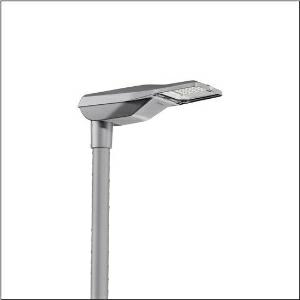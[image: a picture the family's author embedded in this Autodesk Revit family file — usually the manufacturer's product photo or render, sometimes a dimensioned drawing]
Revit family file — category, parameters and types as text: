
# Revit family: streetlight_sl_21_iq_micro___st1_5a_5xe1p41g08cb_60b9
name_source: partatom
category: Lighting Fixtures
units: mm (PartAtom-declared; Revit-internal decimal feet)

## family parameters
Cut with Voids When Loaded = No
Host = Face
Light Source = No
Part Type = Normal
Room Calculation Point = No
Round Connector Dimension = Use Diameter
Shared = No

## types (1)
- --- (1 x LED, 2930 lm, 19.4 W, 4000K)
    Apparent Load = 19 VA
    CIE Flux Codes = 22 53 95 100 100
    Color Rendering = 70
    Color Temperature = 4000K
    Default Elevation = 1800 mm
    Description = Streetlight SL 21 iQ micro, mast luminaire, primary light control with lens, of PMMA, primary optical cover: cover, of toughened safety glass, transparent, light distribution: ST1.5a, light emission: direct distribution, primary light characteristic: asymmetric, installation type: post-top, side-entry, LED, High Power LED, rated luminous flux: 2.930lm, luminous efficacy: 151lm/W, light colour: 740, colour temperature: 4000K, control gear: iQ Street-Remote, control: Street-Remote, Auto-Match, Temp-Guard, Lumen-Switch, Night-Set, Smart-Wire, Light-Fading, Desk-Remote (wireless, voltage-free reading and setting of iQ features in the workshop via application-optimized NFC function/RFID function), optimised constant luminous flux control (CLO 2.0), pre-setting: linear dimming characteristic, mains connection: 220..240V, AC, 50/60Hz, start of lifetime: 19W, end of service life: 20W, reduction: 10W, luminaire housing, of diecast aluminium, powder-coated, Siteco® metallic grey (DB 702S), corrosivity category C5 mid according to DIN EN ISO 12944, please order mast flange separately, inclination adjustable: 0°, 5°, 10°, 15°, sealing non-destructively replaceable, multi-level sealing system, length: 528mm, width: 235mm, height: 110mm, mast flange for spigot size: 42mm (side-entry): 5XC10008XM4, 60/48mm (side-entry/post-top): 5XC10108XM2, 76/60mm (side-entry/post-top): 5XC10108XM1, protection rating (complete): IP66, insulation class (complete): insulation class II (safety insulation), certification: CE, ENEC, ENEC+, VDE, impact resistance: IK10, permissible operating ambient temperature for outdoor applications: -40..+50°C, standard-compliant lighting for roads and squares, packaging unit: 1 piece

Light Distribution: ST1.5a
    Height = 110 mm
    Lamp = 1 x LED
    Lamp Light Flux = 2930 lm
    Lamp Power = 19.4 W
    Lamp count = 1
    Length = 528 mm
    Luminous efficacy = 151 lm/W
    Manufacturer = Siteco
    ModVariant = No
    Model = 5XE1P41G08CB
    Number of Poles = 1
    OnlyDefault = Yes
    Power Factor = 1
    Product Name = Streetlight SL 21 iQ micro | ST1.5a
    Product group = mast luminaire | pylon top
    ProductGroupID = 6100
    Protection Class = Protection class II
    Protection Degree = IP 66
    RLX_Detail_Level = 1
    RLX_Emergency_Light_Flux = 0 lm
    RLX_Emergency_Type = 0
    RLX_Emergency_Type_DB = No
    RlxData = <blob elided: 102165 chars, md5=90979f59>
    Socket = socket
    Standby Power = 0 W
    System Light Flux = 2930 lm
    System Power = 19 W
    Type Comments = factory setting: luminous flux: 100 % | dim-lin: 254 | 387 mA
    Type Image = l_1006881.jpg
    URL = http://relux.com
    VarID = @adj_159479
    Voltage = 0 V
    Weight = 0.00 kg
    Width = 235 mm

## geometry (parser evidence)
native form markers: Blend x4, Sweep x10
no freeform markers — native parametric forms only
